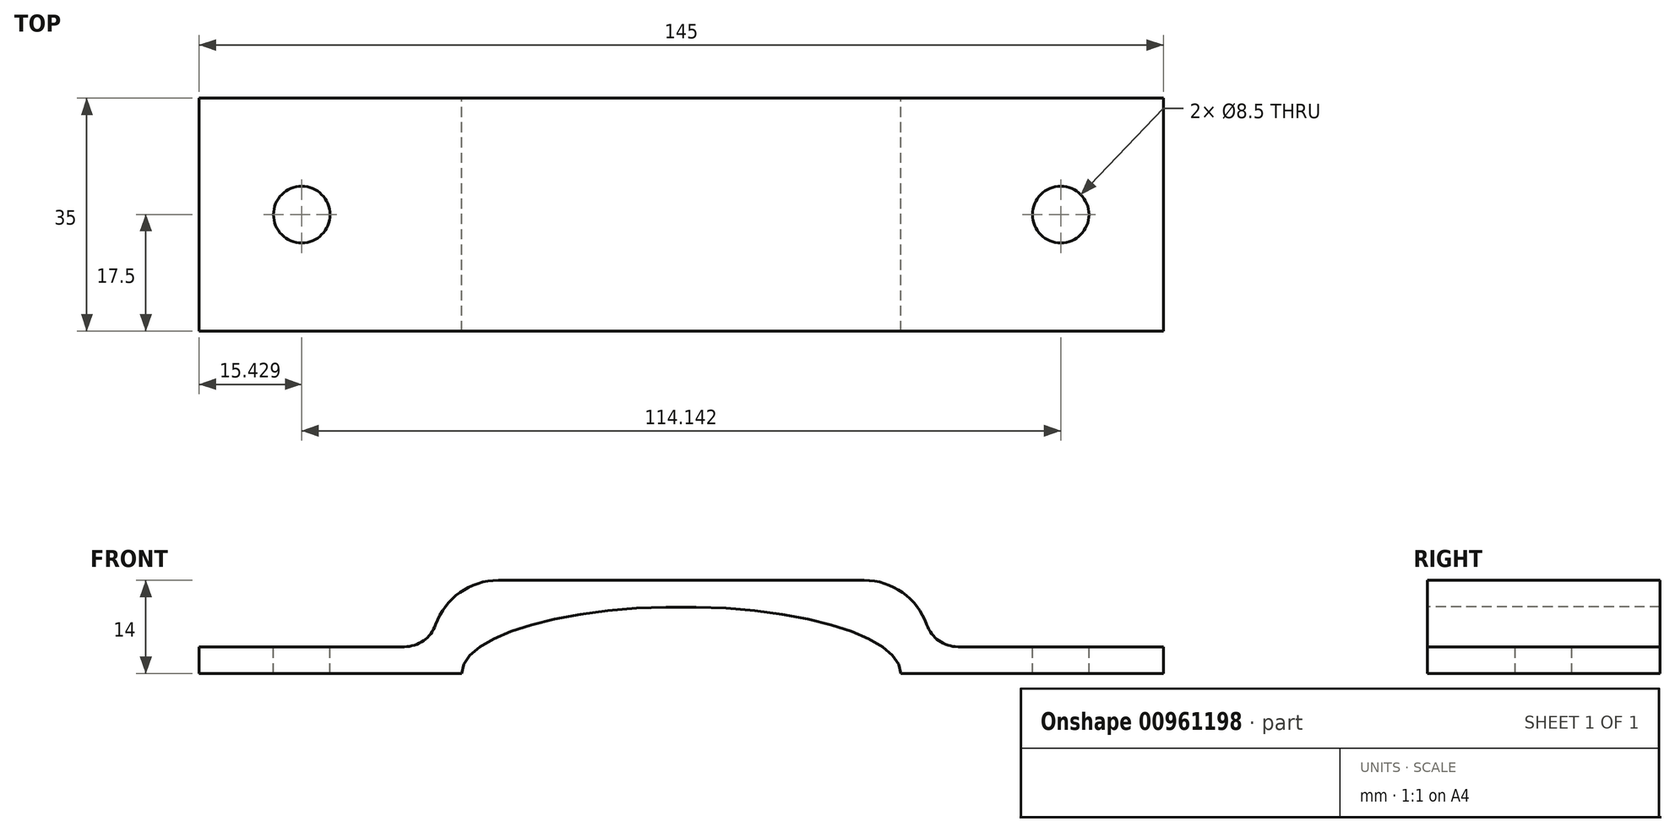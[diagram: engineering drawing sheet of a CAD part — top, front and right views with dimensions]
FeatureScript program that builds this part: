
annotation { "Feature Type Name" : "Feature", "Feature Type Description" : "" }
export const myFeature = defineFeature(function(context is Context, id is Id, definition is map)
    precondition{}
    {
        {
            var Q0;
            Q0=qCreatedBy(makeId("Front.planeOp"),FACE);
            var sketch = newSketch(context, id + "F0", { "sketchPlane" : qUnion([Q0])});
            skEllipticalArc(sketch, "E0", {});
            skLineSegment(sketch, "E1", {"start": v(0, 14) * mm, "end": v(-37.5, 14) * mm});
            skLineSegment(sketch, "E2", {"start": v(-37.5, 14) * mm, "end": v(-37.5, 4) * mm});
            skLineSegment(sketch, "E3", {"start": v(-37.5, 0) * mm, "end": v(-33, 0) * mm});
            skLineSegment(sketch, "E4.MirrorCS", {"start": v(0, 14) * mm, "end": v(37.5, 14) * mm});
            skLineSegment(sketch, "E5.MirrorCS", {"start": v(37.5, 0) * mm, "end": v(33, 0) * mm});
            skLineSegment(sketch, "E6.MirrorCS", {"start": v(37.5, 14) * mm, "end": v(37.5, 4) * mm});
            skLineSegment(sketch, "E7", {"start": v(37.5, 0) * mm, "end": v(72.5, 0) * mm});
            skLineSegment(sketch, "E8", {"start": v(72.5, 0) * mm, "end": v(72.5, 4) * mm});
            skLineSegment(sketch, "E9", {"start": v(72.5, 4) * mm, "end": v(37.5, 4) * mm});
            skLineSegment(sketch, "E10.MirrorCS", {"start": v(-37.5, 0) * mm, "end": v(-72.5, 0) * mm});
            skLineSegment(sketch, "E11.MirrorCS", {"start": v(-72.5, 4) * mm, "end": v(-37.5, 4) * mm});
            skLineSegment(sketch, "E12.MirrorCS", {"start": v(-72.5, 0) * mm, "end": v(-72.5, 4) * mm});
            const initialGuessF0  = {"E0": [0, 0, -1, 0, 0.033, 0.01, 3.141592653589793, 0]};
            skSetInitialGuess(sketch, initialGuessF0);
            skSolve(sketch);
        }
        {
            var Q0;
            Q0=makeQuery(id+"F0.imprint","IMPRINT",FACE,{"disambiguationData":[TD([[makeQuery(id+"F0.imprint","IMPRINT",EDGE,{"derivedFrom":sQuery(id+"F0.wireOp",EDGE,"E0")}),-1.0]])]});
            extrude(context, id + "F1", {"entities" : qUnion([Q0]), "endBound" : BoundingType.SYMMETRIC, "depth" : 35 * mm, "offsetDistance" : 25 * mm});
        }
        {
            var Q0;
            Q0=makeQuery(id+"F1.opExtrude","SWEPT_EDGE",EDGE,{"disambiguationData":[OSD([sQuery(id+"F0.wireOp",EDGE,"E4.MirrorCS"),sQuery(id+"F0.wireOp",EDGE,"E6.MirrorCS")])]});
            var Q1;
            Q1=makeQuery(id+"F1.opExtrude","SWEPT_EDGE",EDGE,{"disambiguationData":[OSD([sQuery(id+"F0.wireOp",EDGE,"E1"),sQuery(id+"F0.wireOp",EDGE,"E2")])]});
            fillet(context, id + "F2", {"entities" : qUnion([Q0, Q1]), "radius" : 10 * mm, "tangentPropagation" : true, "allowEdgeOverflow" : false});
        }
        {
            var Q0;
            Q0=makeQuery(id+"F2.opFillet","BLEND_EDGE",EDGE,{"blendedFrom":[makeQuery(id+"F1.opExtrude","SWEPT_EDGE",EDGE,{"disambiguationData":[OSD([sQuery(id+"F0.wireOp",EDGE,"E1"),sQuery(id+"F0.wireOp",EDGE,"E2")])]}),makeQuery(id+"F1.opExtrude","SWEPT_FACE",FACE,{"disambiguationData":[OSD([sQuery(id+"F0.wireOp",EDGE,"E11.MirrorCS")])]})],"blendedInto":[makeQuery(id+"F1.opExtrude","SWEPT_FACE",FACE,{"disambiguationData":[OSD([sQuery(id+"F0.wireOp",EDGE,"E11.MirrorCS")])]})]});
            var Q1;
            Q1=makeQuery(id+"F2.opFillet","BLEND_EDGE",EDGE,{"blendedFrom":[makeQuery(id+"F1.opExtrude","SWEPT_EDGE",EDGE,{"disambiguationData":[OSD([sQuery(id+"F0.wireOp",EDGE,"E4.MirrorCS"),sQuery(id+"F0.wireOp",EDGE,"E6.MirrorCS")])]}),makeQuery(id+"F1.opExtrude","SWEPT_FACE",FACE,{"disambiguationData":[OSD([sQuery(id+"F0.wireOp",EDGE,"E9")])]})],"blendedInto":[makeQuery(id+"F1.opExtrude","SWEPT_FACE",FACE,{"disambiguationData":[OSD([sQuery(id+"F0.wireOp",EDGE,"E9")])]})]});
            fillet(context, id + "F3", {"entities" : qUnion([Q0, Q1]), "radius" : 5 * mm, "tangentPropagation" : true, "allowEdgeOverflow" : false});
        }
        {
            var Q0;
            Q0=makeQuery(id+"F1.opExtrude","SWEPT_FACE",FACE,{"disambiguationData":[OSD([sQuery(id+"F0.wireOp",EDGE,"E9")])]});
            var sketch = newSketch(context, id + "F4", { "sketchPlane" : qUnion([Q0])});
            skCircle(sketch, "E13", {"center": v(57.07, 0) * mm, "radius": 4.25 * mm});
            skPoint(sketch, "E13.centerSnap0", {"position": v(72.5, 0) * mm});
            skPoint(sketch, "E13.centerSnap1", {"position": v(57.07, 17.5) * mm});
            skCircle(sketch, "E14.MirrorC", {"center": v(-57.07, 0) * mm, "radius": 4.25 * mm});
            skSolve(sketch);
        }
        {
            var Q0;
            Q0 = qSketchRegion(id + "F4", true);
            extrude(context, id + "F5", {"entities" : qUnion([Q0]), "operationType" : NewBodyOperationType.REMOVE, "oppositeDirection" : true, "depth" : 25 * mm, "offsetDistance" : 25 * mm});
        }
    });
